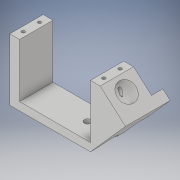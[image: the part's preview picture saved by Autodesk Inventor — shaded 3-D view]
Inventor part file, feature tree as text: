
AUTODESK INVENTOR PART (.ipt)
format: ipt  version: 2019 (Build 230136000, 136)  size: 181,760 bytes
history: native  units: mm
features: extrude x6, sketch x5, other x1
ambient origin geometry x8: Origin, YZ Plane, XZ Plane, XY Plane, X Axis, Y Axis, Z Axis, Center Point
bodies: Body1 (feature_tree)
feature tree (12):
  other  "Твердое тело1"
  extrude  "Выдавливание1"  Depth=5.0mm
  extrude  "Выдавливание2"  Depth=6.0mm
  sketch  "Эскиз3"
  extrude  "Выдавливание3"  Depth=43.5mm
  extrude  "Выдавливание4"  Depth=6.0mm
  extrude  "Выдавливание5"  Depth=38.0mm
  extrude  "Выдавливание6"  Depth=38.0mm
  sketch  "Эскиз1"
  sketch  "Эскиз2"
  sketch  "Эскиз4"
  sketch  "Эскиз5"
